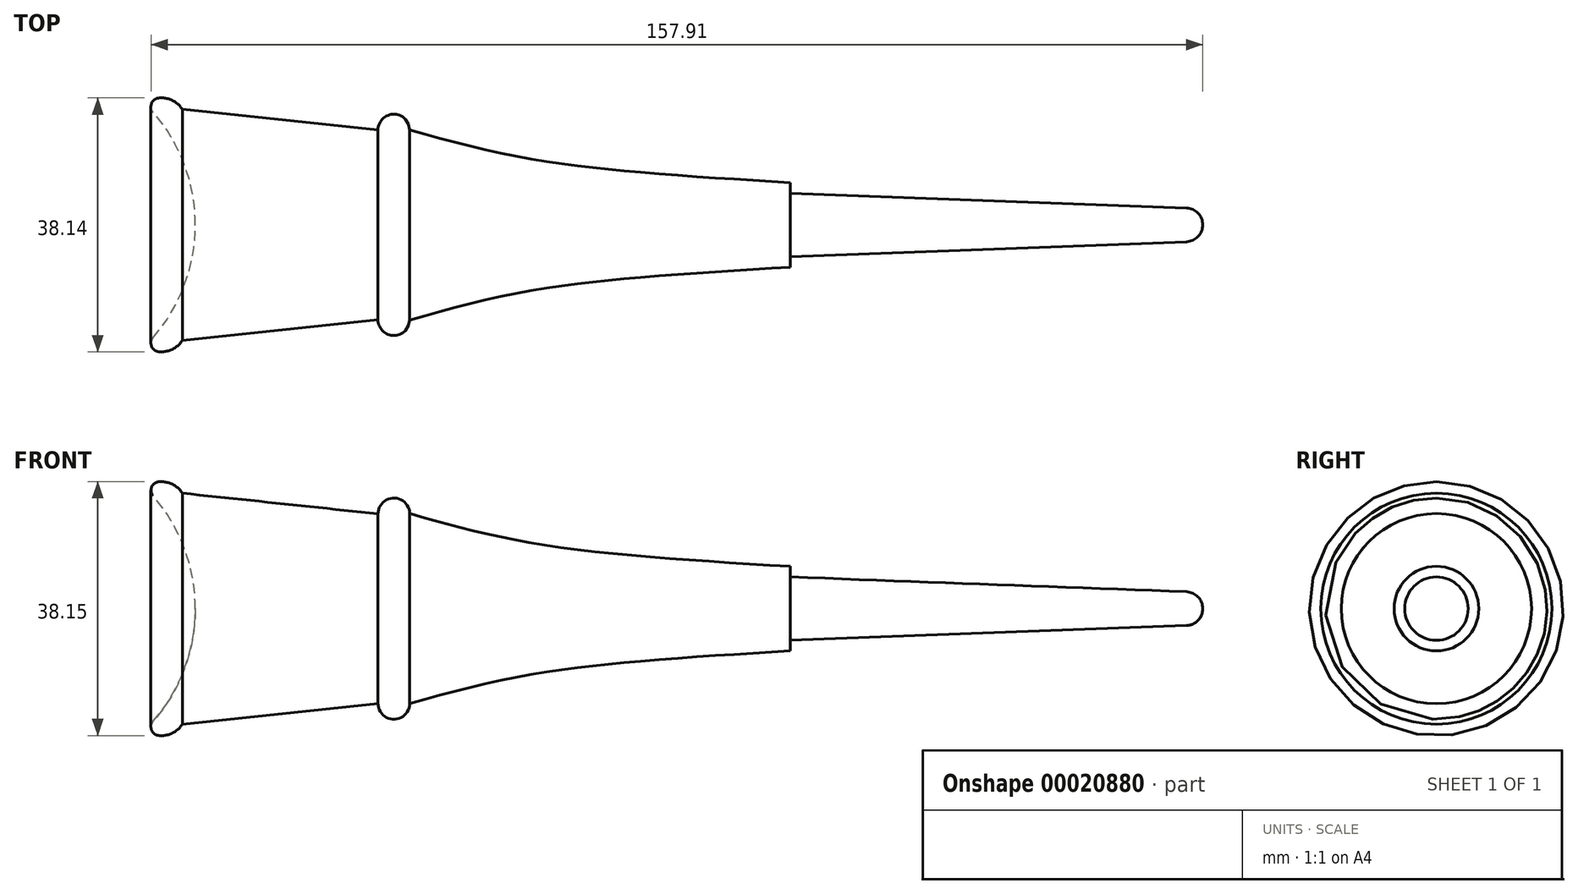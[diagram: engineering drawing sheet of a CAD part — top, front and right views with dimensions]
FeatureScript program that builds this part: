
annotation { "Feature Type Name" : "Feature", "Feature Type Description" : "" }
export const myFeature = defineFeature(function(context is Context, id is Id, definition is map)
    precondition{}
    {
        {
            var Q0;
            Q0=qCreatedBy(makeId("Front.planeOp"),FACE);
            var sketch = newSketch(context, id + "F0", { "sketchPlane" : qUnion([Q0])});
            skPoint(sketch, "E0.start.orphan", {"position": v(-58.76, -3.27) * mm});
            skPoint(sketch, "E1.visualSharp", {"position": v(99.99, -0.82) * mm});
            skLineSegment(sketch, "E2.left", {"start": v(99.99, -3.27) * mm, "end": v(99.99, -3.27) * mm});
            skPoint(sketch, "E3.visualSharp", {"position": v(-58.78, 14.95) * mm});
            skLineSegment(sketch, "E2.bottom", {"start": v(99.99, -3.27) * mm, "end": v(38.07, -3.27) * mm});
            skLineSegment(sketch, "E2.top", {"start": v(97.54, -0.73) * mm, "end": v(38.07, 1.5) * mm});
            skPoint(sketch, "E0.end.orphan", {"position": v(-51.27, -3.27) * mm});
            skLineSegment(sketch, "E4", {"start": v(-34.83, -3.27) * mm, "end": v(-34.83, 12.13) * mm, "construction": true});
            skFitSpline(sketch, "E5", {"points": [v(38.07, 3.08) * mm, v(0.4, 6.4) * mm, v(-19.08, 11.02) * mm], "startDerivative": vector(-70.52, 4.23) * mm, "endDerivative": vector(-42.3, 12.05) * mm});
            skArc(sketch, "E6", {"start": v(-19.08, 11.02) * mm, "mid": v(-21.48, 13.35) * mm, "end": v(-23.84, 10.97) * mm});
            skLineSegment(sketch, "E7", {"start": v(-53.2, 14.08) * mm, "end": v(-23.84, 10.97) * mm});
            skArc(sketch, "E8", {"start": v(-53.2, 14.08) * mm, "mid": v(-54.75, 15.44) * mm, "end": v(-56.8, 15.78) * mm});
            skArc(sketch, "E9", {"start": v(-51.27, -3.27) * mm, "mid": v(-52.9, 5.78) * mm, "end": v(-57.61, 13.69) * mm});
            skLineSegment(sketch, "E10", {"start": v(-51.27, -3.27) * mm, "end": v(99.99, -3.27) * mm});
            skLineSegment(sketch, "E2.right", {"start": v(38.07, -3.27) * mm, "end": v(38.07, 1.5) * mm, "construction": true});
            skArc(sketch, "E1.filletArc", {"start": v(99.99, -3.27) * mm, "mid": v(99.27, -1.5) * mm, "end": v(97.54, -0.73) * mm});
            skArc(sketch, "E3.filletArc", {"start": v(-56.8, 15.78) * mm, "mid": v(-57.83, 14.98) * mm, "end": v(-57.61, 13.69) * mm});
            skLineSegment(sketch, "E11", {"start": v(38.07, 1.5) * mm, "end": v(38.07, 3.08) * mm});
            skSolve(sketch);
        }
        {
            var Q0;
            Q0=makeQuery(id+"F0.imprint","IMPRINT",FACE,{"disambiguationData":[TD([[makeQuery(id+"F0.imprint","IMPRINT",EDGE,{"derivedFrom":sQuery(id+"F0.wireOp",EDGE,"E2.top")}),1.0]])]});
            var Q1;
            Q1=sQuery(id+"F0.wireOp",EDGE,"E10");
            revolve(context, id + "F1", {"entities" : qUnion([Q0]), "axis" : qUnion([Q1]), "revolveType" : RevolveType.FULL});
        }
    });
